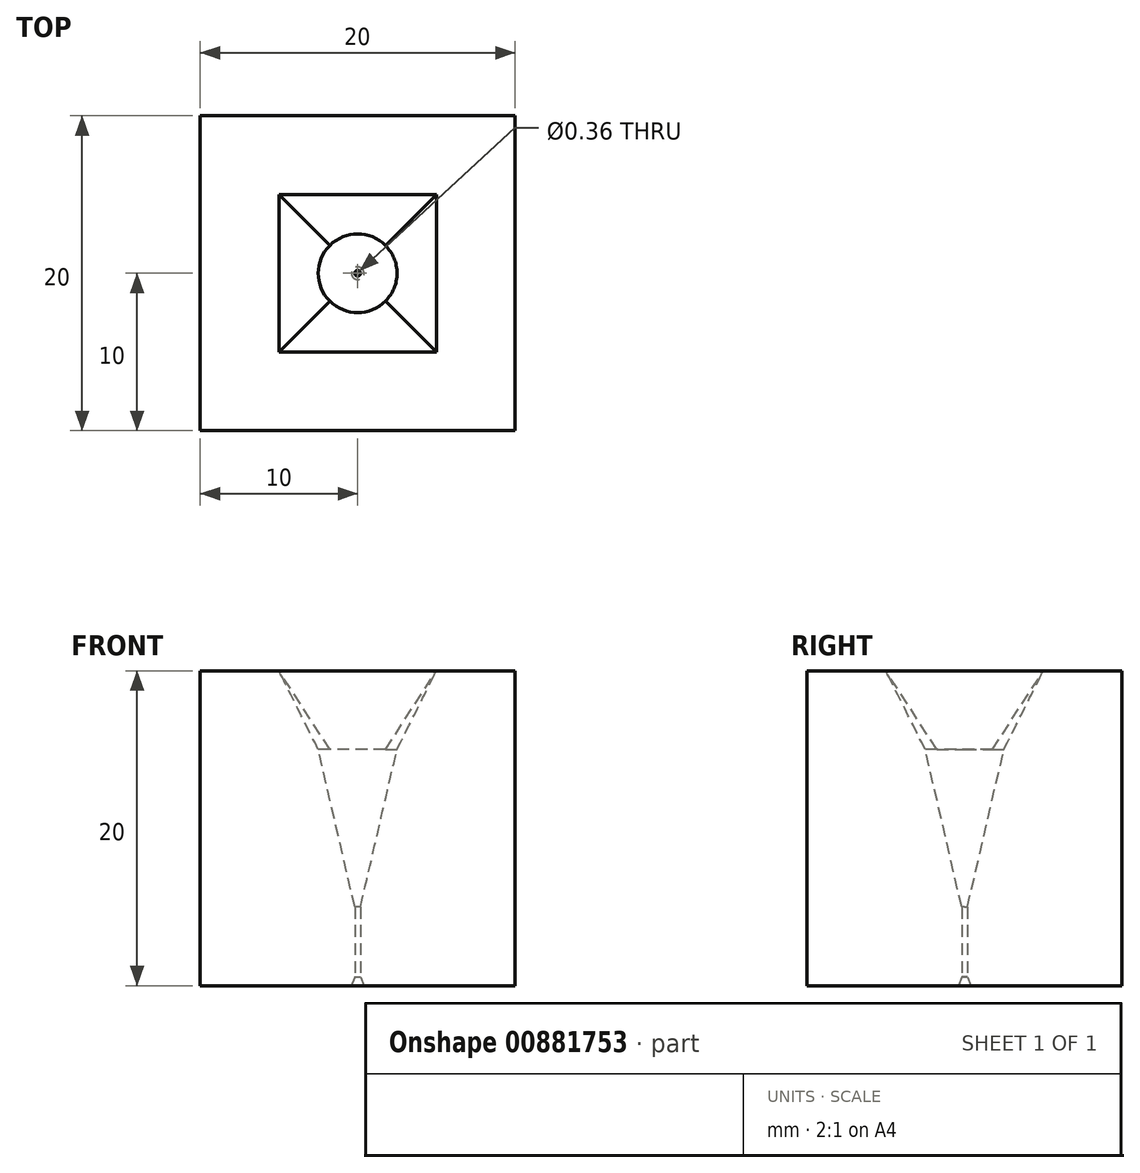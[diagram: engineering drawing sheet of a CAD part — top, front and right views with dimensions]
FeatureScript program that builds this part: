
annotation { "Feature Type Name" : "Feature", "Feature Type Description" : "" }
export const myFeature = defineFeature(function(context is Context, id is Id, definition is map)
    precondition{}
    {
        {
            var Q0;
            Q0=qCreatedBy(makeId("Top.planeOp"),FACE);
            var sketch = newSketch(context, id + "F0", { "sketchPlane" : qUnion([Q0])});
            skLineSegment(sketch, "E0.bottom", {"start": v(-10, 10) * mm, "end": v(10, 10) * mm});
            skLineSegment(sketch, "E0.top", {"start": v(-10, -10) * mm, "end": v(10, -10) * mm});
            skLineSegment(sketch, "E0.left", {"start": v(-10, 10) * mm, "end": v(-10, -10) * mm});
            skLineSegment(sketch, "E0.right", {"start": v(10, 10) * mm, "end": v(10, -10) * mm});
            skLineSegment(sketch, "E1", {"start": v(0, 10) * mm, "end": v(0, -10) * mm, "construction": true});
            skLineSegment(sketch, "E2", {"start": v(-10, 0) * mm, "end": v(10, 0) * mm, "construction": true});
            skCircle(sketch, "E3", {"center": v(0, 0) * mm, "radius": 0.18 * mm});
            skSolve(sketch);
        }
        {
            var Q0;
            Q0=makeQuery(id+"F0.imprint","IMPRINT",FACE,{"disambiguationData":[TD([[makeQuery(id+"F0.imprint","IMPRINT",EDGE,{"derivedFrom":sQuery(id+"F0.wireOp",EDGE,"E0.bottom")}),-1.0]])]});
            extrude(context, id + "F1", {"entities" : qUnion([Q0]), "depth" : 20 * mm, "offsetDistance" : 25 * mm});
        }
        {
            var Q0;
            Q0=makeQuery(id+"F1.opExtrude","CAP_FACE",FACE,{"disambiguationData":[OSD([sQuery(id+"F0.wireOp",EDGE,"E0.bottom"),sQuery(id+"F0.wireOp",EDGE,"E0.top"),sQuery(id+"F0.wireOp",EDGE,"E0.left"),sQuery(id+"F0.wireOp",EDGE,"E0.right"),sQuery(id+"F0.wireOp",EDGE,"E3")])],"isStart":false});
            var sketch = newSketch(context, id + "F2", { "sketchPlane" : qUnion([Q0])});
            skLineSegment(sketch, "E4.bottom", {"start": v(-5, 5) * mm, "end": v(5, 5) * mm});
            skLineSegment(sketch, "E4.top", {"start": v(-5, -5) * mm, "end": v(5, -5) * mm});
            skLineSegment(sketch, "E4.left", {"start": v(-5, 5) * mm, "end": v(-5, -5) * mm});
            skLineSegment(sketch, "E4.right", {"start": v(5, 5) * mm, "end": v(5, -5) * mm});
            skSolve(sketch);
        }
        {
            var Q0;
            Q0=makeQuery(id+"F2.imprint","IMPRINT",FACE,{"disambiguationData":[TD([[makeQuery(id+"F2.imprint","IMPRINT",EDGE,{"derivedFrom":sQuery(id+"F2.wireOp",EDGE,"E4.bottom")}),1.0]])]});
            cPlane(context, id + "F3", {"entities" : qUnion([Q0]), "cplaneType" : CPlaneType.OFFSET, "offset" : 5 * mm, "oppositeDirection" : true, "width" : 150 * mm, "height" : 150 * mm});
        }
        {
            var Q0;
            Q0=qCreatedBy(id+"F3.planeOp",FACE);
            var sketch = newSketch(context, id + "F4", { "sketchPlane" : qUnion([Q0])});
            skCircle(sketch, "E5", {"center": v(0, 0) * mm, "radius": 2.5 * mm});
            skSolve(sketch);
        }
        {
            var Q0;
            Q0=qCreatedBy(id+"F3.planeOp",FACE);
            cPlane(context, id + "F5", {"entities" : qUnion([Q0]), "cplaneType" : CPlaneType.OFFSET, "offset" : 10 * mm, "oppositeDirection" : true, "width" : 150 * mm, "height" : 150 * mm});
        }
        {
            var Q0;
            Q0=qCreatedBy(id+"F5.planeOp",FACE);
            var sketch = newSketch(context, id + "F6", { "sketchPlane" : qUnion([Q0])});
            skCircle(sketch, "E6", {"center": v(0, 0) * mm, "radius": 0.18 * mm});
            skSolve(sketch);
        }
        {
            var Q1;
            Q1 = qSketchRegion(id + "F4", true);
            var Q2;
            Q2 = qSketchRegion(id + "F2", true);
            loft(context, id + "F7", {"operationType" : NewBodyOperationType.REMOVE, "sheetProfilesArray" : [{ "sheetProfileEntities" : qUnion([Q1]) }, { "sheetProfileEntities" : qUnion([Q2]) }]});
        }
        {
            var Q1;
            Q1 = qSketchRegion(id + "F4", true);
            var Q2;
            Q2 = qSketchRegion(id + "F6", true);
            loft(context, id + "F8", {"operationType" : NewBodyOperationType.REMOVE, "sheetProfilesArray" : [{ "sheetProfileEntities" : qUnion([Q1]) }, { "sheetProfileEntities" : qUnion([Q2]) }]});
        }
        {
            var Q0;
            Q0=makeQuery(id+"F1.opExtrude","SWEPT_FACE",FACE,{"disambiguationData":[OSD([sQuery(id+"F0.wireOp",EDGE,"E0.left")])]});
            cPlane(context, id + "F9", {"entities" : qUnion([Q0]), "cplaneType" : CPlaneType.OFFSET, "offset" : 10 * mm, "oppositeDirection" : true, "width" : 150 * mm, "height" : 150 * mm});
        }
        {
            var Q0;
            Q0=qCreatedBy(id+"F9.planeOp",FACE);
            var sketch = newSketch(context, id + "F10", { "sketchPlane" : qUnion([Q0])});
            skLineSegment(sketch, "E7", {"start": v(0, 1) * mm, "end": v(0.4, 0) * mm});
            skLineSegment(sketch, "E8", {"start": v(0.4, 0) * mm, "end": v(0, 0) * mm});
            skLineSegment(sketch, "E9", {"start": v(0, 0) * mm, "end": v(0, 1) * mm});
            skSolve(sketch);
        }
        {
            var Q0;
            Q0 = qSketchRegion(id + "F10", true);
            var Q1;
            Q1=sQuery(id+"F10.wireOp",EDGE,"E9");
            revolve(context, id + "F11", {"operationType" : NewBodyOperationType.REMOVE, "surfaceOperationType" : NewSurfaceOperationType.NEW, "entities" : qUnion([Q0]), "axis" : qUnion([Q1]), "revolveType" : RevolveType.FULL, "oppositeDirection" : true});
        }
    });
